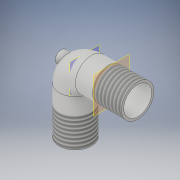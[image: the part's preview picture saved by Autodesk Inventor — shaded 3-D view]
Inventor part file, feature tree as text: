
AUTODESK INVENTOR PART (.ipt)
format: ipt  version: 2018 (Build 220112000, 112)  size: 787,968 bytes
history: native  units: in
note: dims shown in document units (in); Inventor stores cm internally (conversion verified against a paired STEP export)
features: sketch x7, extrude x6, plane x3, thread x2, other x1, chamfer x1
ambient origin geometry x8: Origin, YZ Plane, XZ Plane, XY Plane, X Axis, Y Axis, Z Axis, Center Point
bodies: Body1 (feature_tree)
feature tree (20):
  extrude  "Extrusion5"  Depth=0.5515in
  other  "Bend Part2"
  thread  "Thread3"  [1 undecoded]
  thread  "Thread4"  [1 undecoded]
  plane  "Work Plane3"
  extrude  "Extrusion6"  Depth=0.276in TaperAngle=90.0deg
  plane  "Work Plane4"
  extrude  "Extrusion7"  Depth=0.5in TaperAngle=0.0deg
  chamfer  "Chamfer2"  Distance=29.5276in Angle=360.0deg
  plane  "Work Plane5"
  extrude  "Extrusion8"  TaperAngle=0.0deg  [1 undecoded]
  extrude  "Extrusion9"  Depth=0.285in TaperAngle=45.0deg
  extrude  "Extrusion10"  TaperAngle=0.0deg  [1 undecoded]
  sketch  "Sketch6"  dims[d24=0.475in d25=0.5515in d26=2.0in d27=0.0in d28=2.0in]
  sketch  "Sketch7"  dims[d29=1.0in d30=0.276in d31=90.0deg]
  sketch  "Sketch8"  dims[d32=0.5in d33=0.0in d34=0.5in d35=0.0in]
  sketch  "Sketch9"  dims[d36=-0.45in]
  sketch  "Sketch10"  dims[d37=0.46in d38=29.5276in d40=360.0deg]
  sketch  "Sketch11"  dims[d42=0.45in d43=0.0in d44=0.0in]
  sketch  "Sketch12"  dims[d45=0.1in d46=0.0in d47=0.0925in d48=0.125in d49=45.0deg d50=0.0in d51=0.2in d52=0.3in d53=0.0in d54=0.075in d55=0.3in d56=0.0in d57=0.19in d58=0.285in d59=0.0in]
note: 4 required parameter values undecoded (feature->parameter linkage not recoverable at this tier; creation-order binding heuristic only, values carry confidence <= 0.55)
